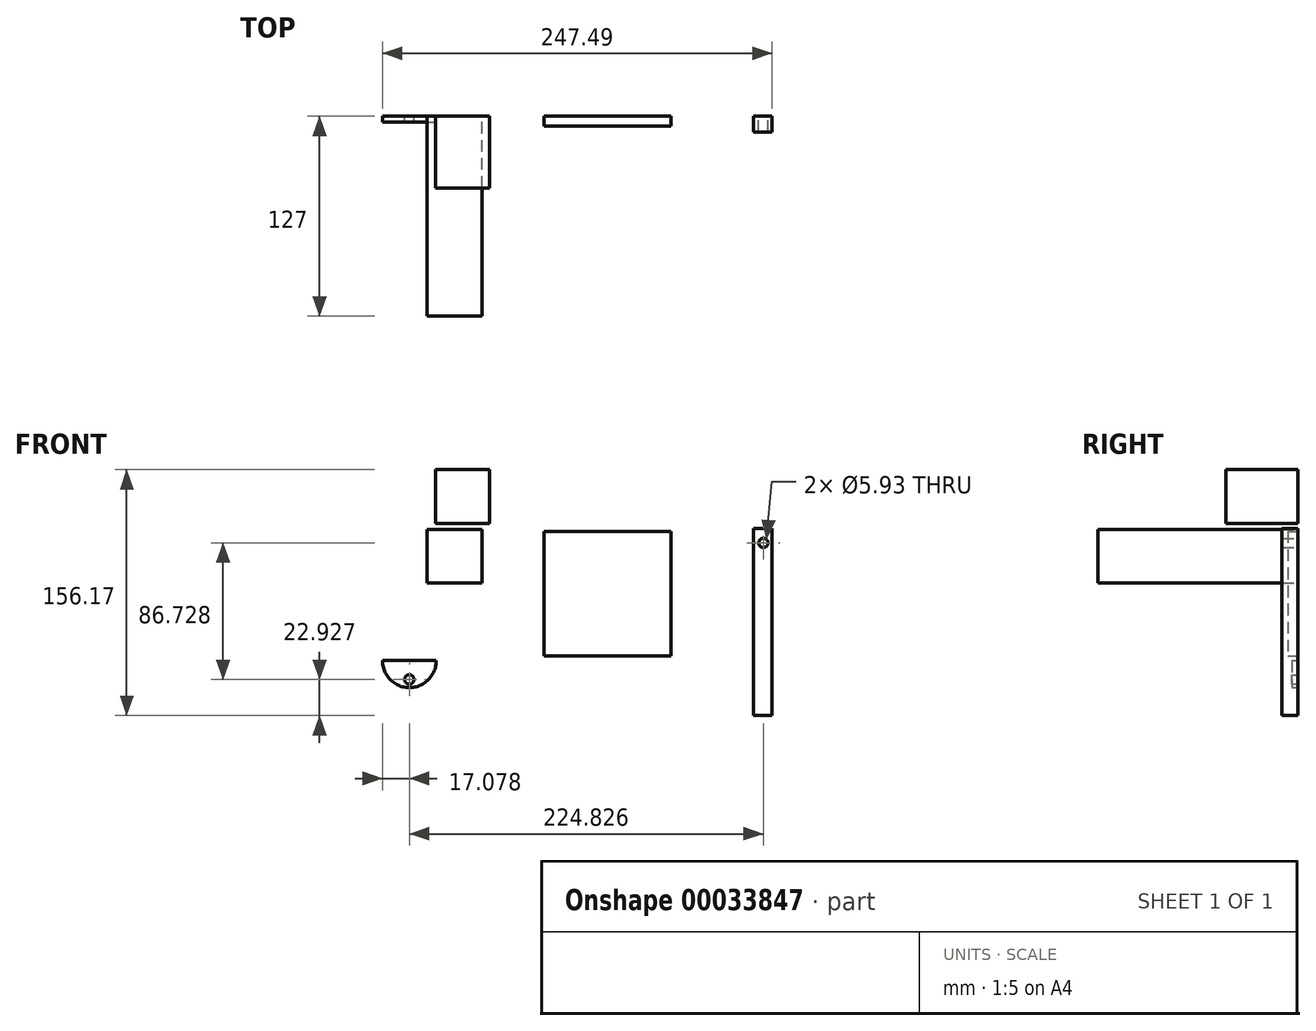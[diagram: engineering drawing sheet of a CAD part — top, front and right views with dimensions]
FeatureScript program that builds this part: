
annotation { "Feature Type Name" : "Feature", "Feature Type Description" : "" }
export const myFeature = defineFeature(function(context is Context, id is Id, definition is map)
    precondition{}
    {
        {
            var Q0;
            Q0=qCreatedBy(makeId("Front.planeOp"),FACE);
            var sketch = newSketch(context, id + "F0", { "sketchPlane" : qUnion([Q0])});
            skLineSegment(sketch, "E0.rect.bottom", {"start": v(-40.31, 39.6) * mm, "end": v(40.31, 39.6) * mm});
            skLineSegment(sketch, "E0.rect.top", {"start": v(-40.31, -39.6) * mm, "end": v(40.31, -39.6) * mm});
            skLineSegment(sketch, "E0.rect.left", {"start": v(-40.31, 39.6) * mm, "end": v(-40.31, -39.6) * mm});
            skLineSegment(sketch, "E0.rect.right", {"start": v(40.31, 39.6) * mm, "end": v(40.31, -39.6) * mm});
            skPoint(sketch, "E0.rect.middle", {"position": v(0, 0) * mm});
            skSolve(sketch);
        }
        {
            var Q0;
            Q0 = qSketchRegion(id + "F0", true);
            extrude(context, id + "F1", {"entities" : qUnion([Q0]), "depth" : 6.35 * mm});
        }
        {
            var Q0;
            Q0=qCreatedBy(makeId("Front.planeOp"),FACE);
            var sketch = newSketch(context, id + "F2", { "sketchPlane" : qUnion([Q0])});
            skLineSegment(sketch, "E1.bottom", {"start": v(-114.52, 40.85) * mm, "end": v(-79.63, 40.85) * mm});
            skLineSegment(sketch, "E1.top", {"start": v(-114.52, 6.7) * mm, "end": v(-79.63, 6.7) * mm});
            skLineSegment(sketch, "E1.left", {"start": v(-114.52, 40.85) * mm, "end": v(-114.52, 6.7) * mm});
            skLineSegment(sketch, "E1.right", {"start": v(-79.63, 40.85) * mm, "end": v(-79.63, 6.7) * mm});
            skLineSegment(sketch, "E2.bottom", {"start": v(-118.52, -84.1) * mm, "end": v(-118.52, -84.1) * mm});
            skLineSegment(sketch, "E2.top", {"start": v(-130.58, -84.1) * mm, "end": v(-118.52, -84.1) * mm});
            skSolve(sketch);
        }
        {
            var Q0;
            Q0 = qSketchRegion(id + "F2", true);
            extrude(context, id + "F3", {"entities" : qUnion([Q0]), "depth" : 127 * mm});
        }
        {
            var Q0;
            Q0=qCreatedBy(makeId("Front.planeOp"),FACE);
            var sketch = newSketch(context, id + "F4", { "sketchPlane" : qUnion([Q0])});
            skLineSegment(sketch, "E3", {"start": v(-142.87, -42.6) * mm, "end": v(-108.71, -42.6) * mm});
            skArc(sketch, "E4", {"start": v(-142.87, -42.6) * mm, "mid": v(-125.8, -59.77) * mm, "end": v(-108.71, -42.6) * mm});
            skCircle(sketch, "E5", {"center": v(-125.8, -54.56) * mm, "radius": 2.96 * mm});
            skSolve(sketch);
        }
        {
            var Q0;
            Q0=makeQuery(id+"F4.imprint","IMPRINT",FACE,{"disambiguationData":[TD([[makeQuery(id+"F4.imprint","IMPRINT",EDGE,{"derivedFrom":sQuery(id+"F4.wireOp",EDGE,"E3")}),-1.0]])]});
            extrude(context, id + "F5", {"entities" : qUnion([Q0]), "depth" : 3.8 * mm});
        }
        {
            var Q0;
            Q0=qCreatedBy(makeId("Front.planeOp"),FACE);
            var sketch = newSketch(context, id + "F6", { "sketchPlane" : qUnion([Q0])});
            skLineSegment(sketch, "E6.bottom", {"start": v(-109.1, 78.68) * mm, "end": v(-74.94, 78.68) * mm});
            skLineSegment(sketch, "E6.top", {"start": v(-109.1, 44.52) * mm, "end": v(-74.94, 44.52) * mm});
            skLineSegment(sketch, "E6.left", {"start": v(-109.1, 78.68) * mm, "end": v(-109.1, 44.52) * mm});
            skLineSegment(sketch, "E6.right", {"start": v(-74.94, 78.68) * mm, "end": v(-74.94, 44.52) * mm});
            skSolve(sketch);
        }
        {
            var Q0;
            Q0 = qSketchRegion(id + "F6", true);
            extrude(context, id + "F7", {"entities" : qUnion([Q0]), "depth" : 45.48 * mm});
        }
        {
            var Q0;
            Q0=qCreatedBy(makeId("Front.planeOp"),FACE);
            var sketch = newSketch(context, id + "F8", { "sketchPlane" : qUnion([Q0])});
            skLineSegment(sketch, "E7.bottom", {"start": v(92.87, 41.41) * mm, "end": v(104.62, 41.41) * mm});
            skLineSegment(sketch, "E7.top", {"start": v(92.87, -77.5) * mm, "end": v(104.62, -77.5) * mm});
            skLineSegment(sketch, "E7.left", {"start": v(92.87, 41.41) * mm, "end": v(92.87, -77.5) * mm});
            skLineSegment(sketch, "E7.right", {"start": v(104.62, 41.41) * mm, "end": v(104.62, -77.5) * mm});
            skCircle(sketch, "E8", {"center": v(99.03, 32.17) * mm, "radius": 2.96 * mm});
            skSolve(sketch);
        }
        {
            var Q0;
            Q0 = qSketchRegion(id + "F8", true);
            extrude(context, id + "F9", {"entities" : qUnion([Q0]), "depth" : 9.93 * mm});
        }
    });
